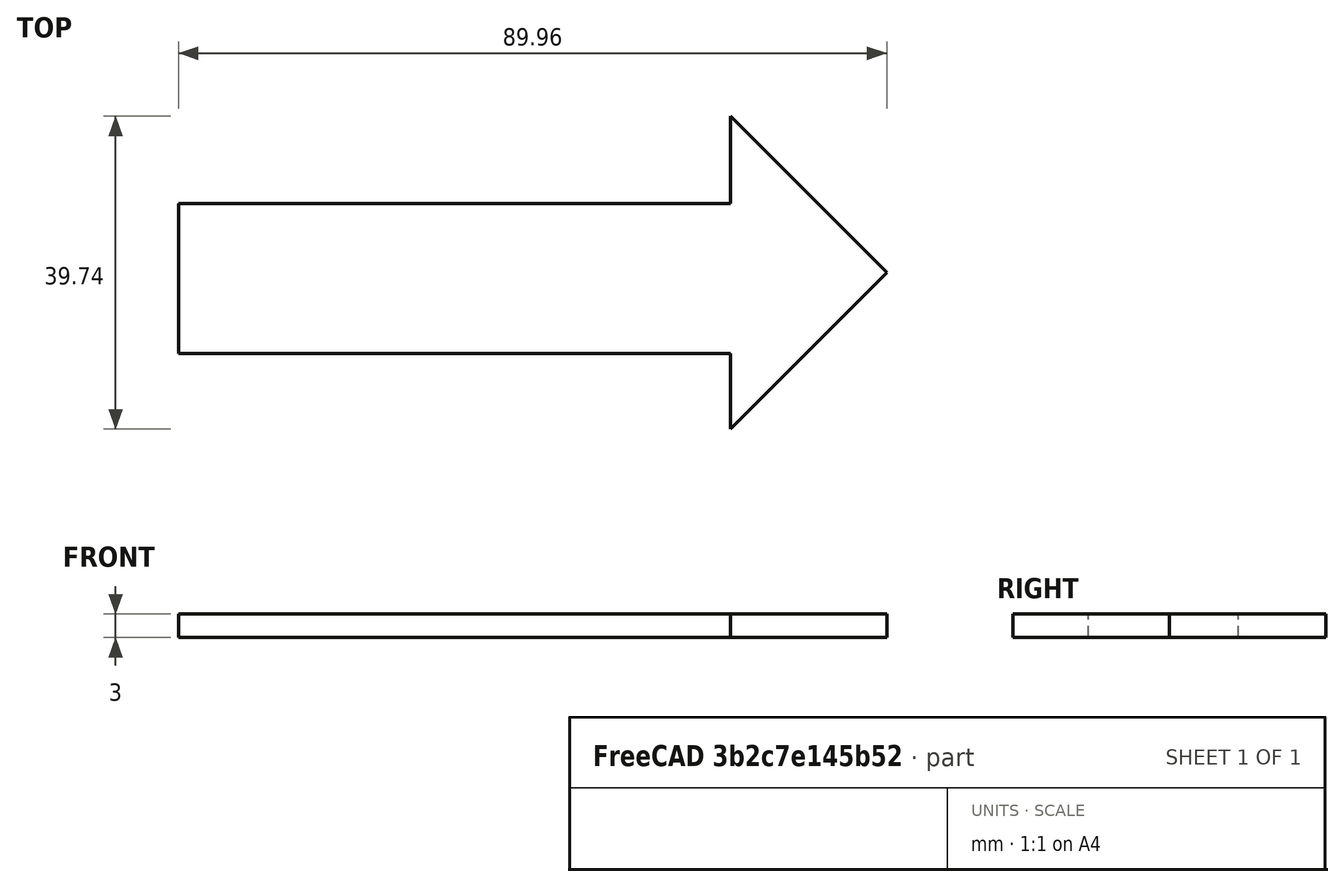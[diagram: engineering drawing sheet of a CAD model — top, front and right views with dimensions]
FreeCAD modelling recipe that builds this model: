
FCSTD DOCUMENT  (FreeCAD 1.0R39319 (Git))
Label: ojt1_t16r02_arrow
License: All rights reserved
LicenseURL: https://en.wikipedia.org/wiki/All_rights_reserved
objects: Sketcher::SketchObject×1, PartDesign::Pad×1, PartDesign::Body×1
note: 6 computed .brp shape members not serialized (recipe doc carries the construction recipe); baked Part::Feature solids carry a one-line shape summary decoded from their .brp

FEATURE [Sketcher::SketchObject] Sketch
  ArcFitTolerance = 1e-06
  AttachmentSupport = -> [XY_Plane]
  FullyConstrained = false
  MakeInternals = false
  MapMode = 5
  sketch-geometry (7):
    g0: LineSegment StartX=-60.1496 StartY=8.76067 StartZ=0 EndX=9.93589 EndY=8.76067 EndZ=0
    g1: LineSegment StartX=9.93589 StartY=8.76067 StartZ=0 EndX=9.93589 EndY=19.8718 EndZ=0
    g2: LineSegment StartX=9.93589 StartY=19.8718 StartZ=0 EndX=29.8077 EndY=0 EndZ=0
    g3: LineSegment StartX=29.8077 StartY=0 StartZ=0 EndX=9.93589 EndY=-19.8718 EndZ=0
    g4: LineSegment StartX=9.93589 StartY=-19.8718 StartZ=0 EndX=9.93589 EndY=-10.2564 EndZ=0
    g5: LineSegment StartX=9.93589 StartY=-10.2564 StartZ=0 EndX=-60.1496 EndY=-10.2564 EndZ=0
    g6: LineSegment StartX=-60.1496 StartY=-10.2564 StartZ=0 EndX=-60.1496 EndY=8.76067 EndZ=0
  constraints (13):
    c: Horizontal(g0)
    c: Coincident(g0,g1)
    c: Vertical(g1)
    c: Coincident(g1,g2)
    c: PointOnObject(g2,g-1)
    c: Coincident(g2,g3)
    c: Coincident(g3,g4)
    c: Vertical(g4)
    c: Coincident(g4,g5)
    c: Horizontal(g5)
    c: Coincident(g5,g6)
    c: Coincident(g6,g0)
    c: Vertical(g6)
FEATURE [PartDesign::Pad] Pad
  Direction = (0,0,1)
  Length = 3
  Length2 = 10
  Profile = -> Sketch
  ReferenceAxis = -> Sketch [N_Axis]
  Refine = true
  Suppressed = false
  Type = 0
FEATURE [PartDesign::Body] Body
  AllowCompound = false
  Group = -> [Sketch,Pad]
  Origin = -> Origin
  Tip = -> Pad
